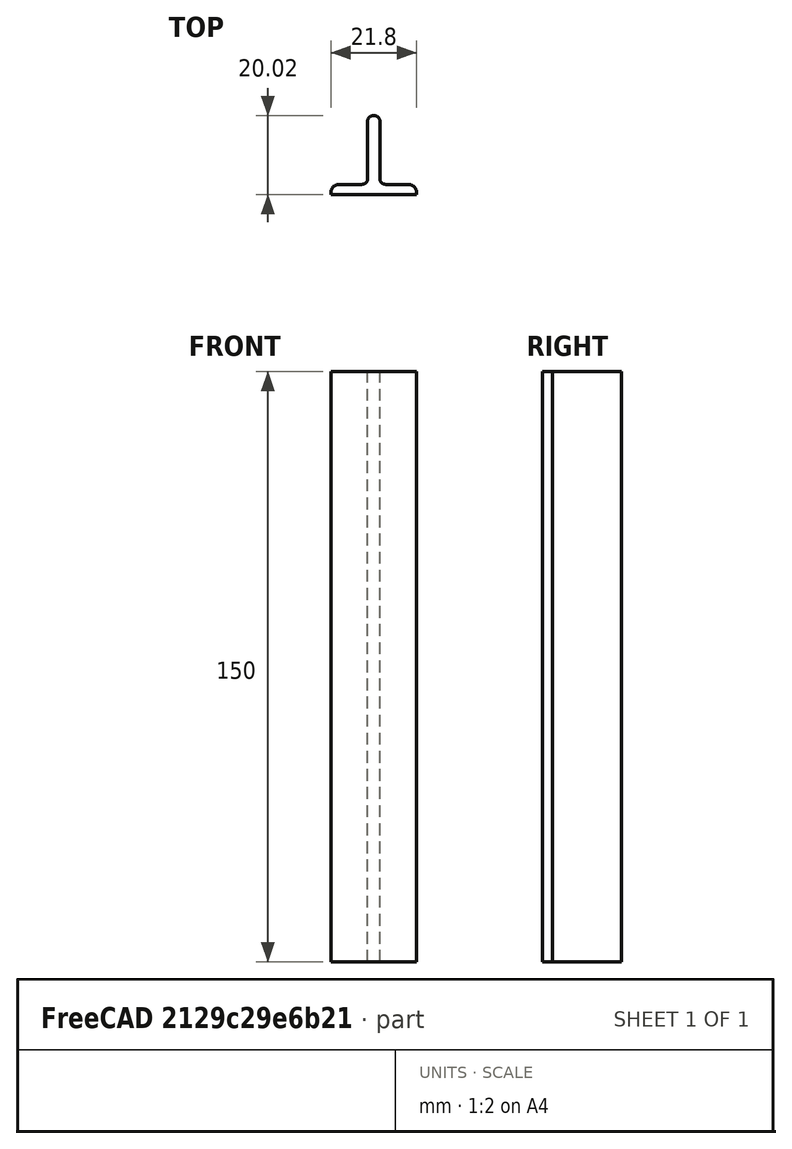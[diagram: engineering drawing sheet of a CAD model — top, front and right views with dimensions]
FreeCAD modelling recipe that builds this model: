
FCSTD DOCUMENT  (FreeCAD 0.18R16146 (Git))
Label: kitty-off-150mm-thinner
License: All rights reserved
LicenseURL: http://en.wikipedia.org/wiki/All_rights_reserved
objects: Sketcher::SketchObject×1, PartDesign::Pad×1, PartDesign::Body×1
note: 4 computed .brp shape members not serialized (recipe doc carries the construction recipe); baked Part::Feature solids carry a one-line shape summary decoded from their .brp

FEATURE [Sketcher::SketchObject] Sketch001
  MapMode = 5
  Support = -> [XY_Plane001]
  sketch-geometry (14):
    g0: LineSegment StartX=-38.0936 StartY=-18.4537 StartZ=0 EndX=-32.2875 EndY=-18.4537 EndZ=0
    g1: LineSegment StartX=-18.3689 StartY=-20.9983 StartZ=0 EndX=-40.1667 EndY=-20.9983 EndZ=0
    g2: LineSegment StartX=-30.8337 StartY=-17 StartZ=0 EndX=-30.8337 EndY=-2.43864 EndZ=0
    g3: LineSegment StartX=-29.38 StartY=-0.984896 StartZ=0 EndX=-29.1555 EndY=-0.984896 EndZ=0
    g4: LineSegment StartX=-27.7018 StartY=-2.43864 StartZ=0 EndX=-27.7018 EndY=-17 EndZ=0
    g5: LineSegment StartX=-26.2481 StartY=-18.4537 StartZ=0 EndX=-20.442 EndY=-18.4537 EndZ=0
    g6: ArcOfCircle CenterX=-29.38 CenterY=-2.43864 CenterZ=0 NormalX=0 NormalY=0 NormalZ=1 AngleXU=0 Radius=1.45374 StartAngle=1.5708 EndAngle=3.14159
    g7: ArcOfCircle CenterX=-29.1555 CenterY=-2.43864 CenterZ=0 NormalX=0 NormalY=0 NormalZ=1 AngleXU=0 Radius=1.45374 StartAngle=0 EndAngle=1.5708
    g8: ArcOfCircle CenterX=-26.2481 CenterY=-17 CenterZ=0 NormalX=0 NormalY=0 NormalZ=1 AngleXU=0 Radius=1.45374 StartAngle=3.14159 EndAngle=4.71239
    g9: ArcOfCircle CenterX=-32.2875 CenterY=-17 CenterZ=0 NormalX=0 NormalY=0 NormalZ=1 AngleXU=0 Radius=1.45374 StartAngle=4.71239 EndAngle=6.28319
    g10: LineSegment StartX=-18.3689 StartY=-20.9983 StartZ=0 EndX=-18.3689 EndY=-20.5268 EndZ=0
    g11: LineSegment StartX=-40.1667 StartY=-20.9983 StartZ=0 EndX=-40.1667 EndY=-20.5268 EndZ=0
    g12: ArcOfCircle CenterX=-38.0936 CenterY=-20.5268 CenterZ=0 NormalX=0 NormalY=0 NormalZ=1 AngleXU=0 Radius=2.07308 StartAngle=1.5708 EndAngle=3.14159
    g13: ArcOfCircle CenterX=-20.442 CenterY=-20.5268 CenterZ=0 NormalX=0 NormalY=0 NormalZ=1 AngleXU=0 Radius=2.07308 StartAngle=4e-16 EndAngle=1.5708
  constraints (29):
    c: Horizontal(g1)
    c: Tangent(g2,g6) = 1.5708
    c: Tangent(g3,g6) = 1.5708
    c: Tangent(g3,g7) = 1.5708
    c: Tangent(g4,g7) = 1.5708
    c: Horizontal(g3)
    c: Vertical(g2)
    c: Vertical(g4)
    c: Equal(g6,g7)
    c: Tangent(g5,g8) = -1.5708
    c: Tangent(g4,g8) = -1.5708
    c: Tangent(g2,g9) = -1.5708
    c: Tangent(g0,g9) = -1.5708
    c: Equal(g9,g8)
    c: Equal(g0,g5)
    c: Horizontal(g0)
    c: Horizontal(g5)
    c: Equal(g11,g10)
    c: Tangent(g11,g12) = 1.5708
    c: Tangent(g0,g12) = 1.5708
    c: Vertical(g11)
    c: Vertical(g10)
    c: Tangent(g5,g13) = 1.5708
    c: Tangent(g10,g13) = -1.5708
    c: Coincident(g11,g1)
    c: Coincident(g1,g10)
    c: Equal(g12,g13)
    c: Equal(g0,g5)
    c: Equal(g9,g6)
FEATURE [PartDesign::Pad] Pad
  Length = 150
  Length2 = 43
  Profile = -> Sketch001
  Type = 0
FEATURE [PartDesign::Body] Body001
  Group = -> [Sketch001,Pad]
  Origin = -> Origin001
  Tip = -> Pad
